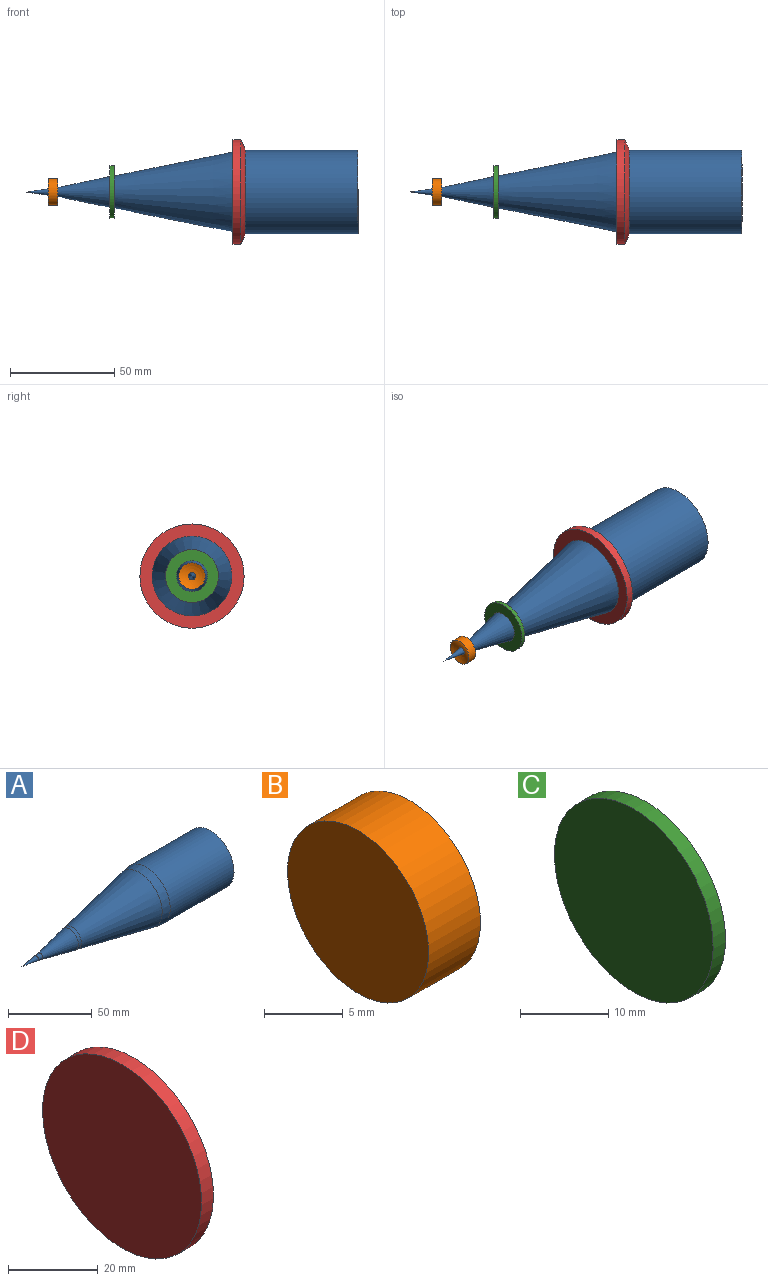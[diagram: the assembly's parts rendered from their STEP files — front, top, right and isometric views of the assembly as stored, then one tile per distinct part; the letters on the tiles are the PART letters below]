
ASSEMBLY  parts=4 mates=6
PART A: 8 faces, bbox 159.3x39.9x39.9 mm
  f0: cone r=7.44mm half-angle=7.9deg, axis (1,0,0), area 102.2mm2, adj f1,f7
  f1: cone r=7.44mm half-angle=11.9deg, axis (1,0,0), area 770.5mm2, adj f0,f2
  f2: cone r=1.72mm half-angle=7.9deg, axis (1,0,0), area 38.3mm2, adj f1,f3
  f3: cone r=1.72mm half-angle=8deg, axis (1,0,0), area 66.6mm2, adj f2
  f4: plane 39.91x39.91mm, normal (1,0,0), area 1251.1mm2, adj f5
  f5: cylinder r=19.96mm len=53.96mm, axis (-1,0,0), area 6765.6mm2, adj f4,f6
  f6: cone r=19.16mm half-angle=7.5deg, axis (1,0,0), area 748.8mm2, adj f5,f7
  f7: cone r=19.16mm half-angle=11.3deg, axis (1,0,0), area 4904.2mm2, adj f0,f6
PART B: 3 faces, bbox 4.7x12.7x12.7 mm
  f0: plane 12.7x12.7mm, normal (-1,0,0), area 126.7mm2, adj f2
  f1: sphere r=12.9mm, area 135.5mm2, adj f2
  f2: cylinder r=6.35mm len=12.7mm, axis (-1,0,0), area 186.4mm2, adj f0,f1
PART C: 3 faces, bbox 2.2x25.4x25.4 mm
  f0: plane 25.4x25.4mm, normal (-1,0,0), area 506.7mm2, adj f2
  f1: sphere r=386.3mm, area 506.8mm2, adj f2
  f2: cylinder r=12.7mm len=25.4mm, axis (-1,0,0), area 158.9mm2, adj f0,f1
PART D: 3 faces, bbox 10x50x50 mm
  f0: plane 50.01x50.01mm, normal (-1,0,0), area 1964.3mm2, adj f2
  f1: revolved ~50.01x50.01mm, area 2085.3mm2, adj f2
  f2: cylinder r=25.01mm len=50.01mm, axis (-1,0,0), area 585.1mm2, adj f0,f1
PLACE A t=(14.14,-7.56,-21.68)mm
PLACE B rot(axis=(0,1,0),180deg) t=(2.63,-7.56,-47.8)mm
PLACE C t=(27.63,-7.56,-47.8)mm
PLACE D t=(89.91,-7.56,-47.8)mm
MATE fastened B.f2 <-> C.f2  axis (1,0,0) through (2.63,-7.56,-47.8)mm
MATE fastened C.f2 <-> D.f2  axis (-1,0,0) through (27.63,-7.56,-47.8)mm
MATE cylindrical A.f0 <-> D.f2  axis (-1,0,0) through (119.69,-7.56,-47.8)mm
MATE cylindrical B.f2 <-> D.f2  axis (1,0,0) through (0.3,-7.56,-47.8)mm
MATE fastened A.f0 <-> D.f2  axis (-1,0,0) through (86.67,-7.56,-47.8)mm
MATE cylindrical B.f2 <-> C.f2  axis (1,0,0) through (-2.04,-7.56,-47.8)mm
